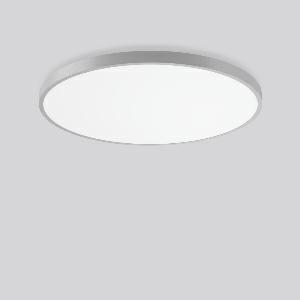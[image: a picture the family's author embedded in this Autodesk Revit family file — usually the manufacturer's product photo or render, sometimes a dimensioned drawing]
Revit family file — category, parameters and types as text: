
# Revit family: triona_round_a_312391_004_2_730_bc95
name_source: partatom
category: Lighting Fixtures
units: mm (PartAtom-declared; Revit-internal decimal feet)

## family parameters
Cut with Voids When Loaded = No
Host = Face
Light Source = No
Part Type = Normal
Room Calculation Point = No
Round Connector Dimension = Use Diameter
Shared = No

## types (1)
- TuneableWhite 846 (1 x LED Modul 846, 5700 lm, 4600)
    Apparent Load = 61 VA
    CIE Flux Codes = 50 80 96 100 100
    Color Rendering = 80
    Color Temperature = 4600
    Default Elevation = 1800 mm
    Description = Series: TRIONA round
Decorative round LED surface-mounted luminaire. Flat, seamless frame: aluminium extrusion profile, powder coated. Cover made of sheet steel, powder-coated. Light emission through a diffuser: plastic, opal. Lightguide and diffuser made of non-yellowing plastic (PMMA). Lateral light emission (RZB SIDELITE technology) for above-average homogeneous light distribution. Tunable white versions, dynamically adjustable from 2700 K to 6500 K. Suitable for Ceiling mounting, Wall (surface). Tool-free mounting via bayonet connection. Electronic ballast included. Very easy installation thanks to Plug+Play connection. With Casambi smart+free Bluetooth control for wireless network and operation using Android / iOS devices, free app available for download. Ideal for use as part of the Human Centric Lighting concept in connection with RZB light management systems. 
Colour: silver, matt (approx. RAL 9006)
Diameter: 1009 mm
Height: 88 mm
Lamp: LED
Socket: without socket
Colour temperature: 2700K - 6500K
Colour rendering index (CRI): 80
System power: 61 W
Rated luminous flux: 5700 lm
Luminous efficiency: 93 lm/W
System power 2: 63 W
Rated luminous flux 2: 5450 lm
Luminous efficiency 2: 87 lm/W
System power 3: 63 W
Rated luminous flux 3: 5500 lm
Luminous efficiency 3: 87 lm/W
Control gear: Dimmable Bluetooth converter
Protection class: I
Type of protection: IP 20
    Height = 88 mm
    Lamp = 1 x LED Modul 846
    Lamp Light Flux = 5700 lm
    Lamp count = 1
    Length = 1009 mm
    Lifetime = 50000 h
    Luminous efficacy = 93 lm/W
    Manufacturer = RZB
    ModVariant = No
    Model = 312391.004.2.730
    Mounting Place = Ceiling
    Mounting Type = Surface mounted
    Number of Poles = 1
    OnlyDefault = Yes
    Power Factor = 1
    Product Name = TRIONA round A
    Product group = Surface mounted modular luminaires
    ProductGroupID = 306
    Protection Class = Protection class I
    Protection Degree = IP 20
    RLX_Detail_Level = 1
    RLX_Emergency_Light_Flux = 0 lm
    RLX_Emergency_Type = 0
    RLX_Emergency_Type_DB = No
    RlxData = <blob elided: 38201 chars, md5=ae3a5c59>
    Socket = socket
    Standby Power = 0 W
    System Light Flux = 5700 lm
    System Power = 61 W
    Type Comments = TuneableWhite 846
    Type Image = 312392.004.jpg
    URL = http://relux.com
    VarID = tuneablewhite_846
    Voltage = 230 V
    Voltage Range = 220-240 V
    Weight = 0.00 kg
    Width = 0 mm  [stored 0 ft]

note: [stored X ft] marks values corroborated as IEEE doubles in the binary element streams (Revit-internal decimal feet)

## geometry (parser evidence)
native form markers: Blend x4, Sweep x9
no freeform markers — native parametric forms only
